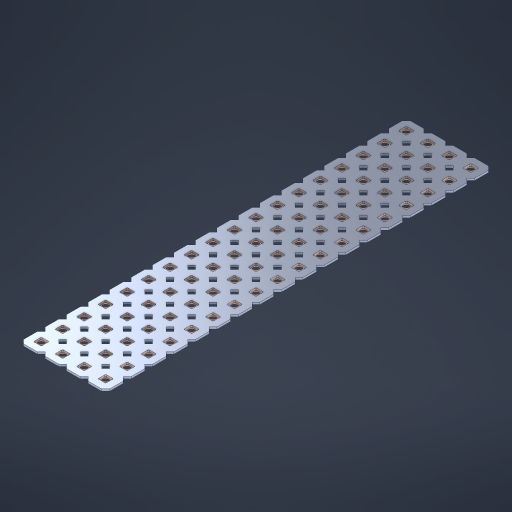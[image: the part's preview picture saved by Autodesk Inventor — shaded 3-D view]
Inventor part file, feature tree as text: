
AUTODESK INVENTOR PART (.ipt)
format: ipt  version: 2023 (Build 270158000, 158)  size: 1,094,144 bytes
history: native  units: in
note: dims shown in document units (in); Inventor stores cm internally (conversion verified against a paired STEP export)
features: other x73, extrude x71, sketch x2, pattern_linear x1
ambient origin geometry x8: Origin, YZ Plane, XZ Plane, XY Plane, X Axis, Y Axis, Z Axis, Center Point
bodies: Solid1 (feature_tree), Body (feature_tree)
feature tree (147):
  pattern_linear  "Rectangular Pattern1"  Spacing1=0.09in  [1 undecoded]
  sketch  "Sketch1"  dims[d1=0.5in]
  sketch  "Sketch2"  dims[d2=0.182in d3=0.09in d4=0.09in d5=0.09in d6=0.09in d7=0.09in d8=0.09in d9=0.09in d10=0.09in d11=0.02in d13=0.0in d14=0.172in d15=0.0625in d16=0.0in d19=0.5in d22=0.5in]
  other  "Srf1"
  other  "Srf126"
  other  "Srf127"
  other  "Srf128"
  other  "Srf129"
  other  "Srf130"
  other  "Srf131"
  other  "Srf250"
  other  "Srf251"
  other  "Srf252"
  other  "Srf253"
  other  "Srf254"
  other  "Srf255"
  other  "Srf256"
  other  "Srf257"
  other  "Srf258"
  other  "Srf259"
  other  "Srf260"
  other  "Srf268"
  other  "Srf269"
  other  "Srf270"
  other  "Srf271"
  other  "Srf272"
  other  "Srf273"
  other  "Srf274"
  other  "Srf275"
  other  "Srf276"
  other  "Srf277"
  other  "Srf278"
  other  "Srf279"
  other  "Srf280"
  other  "Srf281"
  other  "Srf282"
  other  "Srf283"
  other  "Srf284"
  other  "Srf285"
  other  "Srf293"
  other  "Srf294"
  other  "Srf295"
  other  "Srf296"
  other  "Srf297"
  other  "Srf298"
  other  "Srf299"
  other  "Srf300"
  other  "Srf301"
  other  "Srf302"
  other  "Srf303"
  other  "Srf304"
  other  "Srf305"
  other  "Srf306"
  other  "Srf307"
  other  "Srf308"
  other  "Srf309"
  other  "Srf310"
  other  "Srf318"
  other  "Srf319"
  other  "Srf320"
  other  "Srf321"
  other  "Srf322"
  other  "Srf323"
  other  "Srf324"
  other  "Srf325"
  other  "Srf326"
  other  "Srf327"
  other  "Srf328"
  other  "Srf329"
  other  "Srf330"
  other  "Srf331"
  other  "Srf332"
  other  "Srf333"
  other  "Srf334"
  other  "Srf335"
  other  "Circle"
  extrude  "ExtrusionSrf126"  Depth=0.09in
  extrude  "ExtrusionSrf127"  Depth=0.09in
  extrude  "ExtrusionSrf128"  Depth=0.09in
  extrude  "ExtrusionSrf129"  Depth=0.09in
  extrude  "ExtrusionSrf130"  Depth=0.09in
  extrude  "ExtrusionSrf131"  Depth=0.09in
  extrude  "ExtrusionSrf250"  Depth=0.09in
  extrude  "ExtrusionSrf251"  Depth=0.02in
  extrude  "ExtrusionSrf252"  TaperAngle=0.0deg  [1 undecoded]
  extrude  "ExtrusionSrf253"  Depth=0.5in
  extrude  "ExtrusionSrf254"  Depth=0.5in TaperAngle=0.0deg
  extrude  "ExtrusionSrf255"  Depth=0.5in
  extrude  "ExtrusionSrf256"  Depth=0.5in
  extrude  "ExtrusionSrf257"  [1 undecoded]
  extrude  "ExtrusionSrf258"  [1 undecoded]
  extrude  "ExtrusionSrf259"  [1 undecoded]
  extrude  "ExtrusionSrf260"  [1 undecoded]
  extrude  "ExtrusionSrf268"  [1 undecoded]
  extrude  "ExtrusionSrf269"  [1 undecoded]
  extrude  "ExtrusionSrf270"  [1 undecoded]
  extrude  "ExtrusionSrf271"  [1 undecoded]
  extrude  "ExtrusionSrf272"  [1 undecoded]
  extrude  "ExtrusionSrf273"  [1 undecoded]
  extrude  "ExtrusionSrf274"  [1 undecoded]
  extrude  "ExtrusionSrf275"  [1 undecoded]
  extrude  "ExtrusionSrf276"  [1 undecoded]
  extrude  "ExtrusionSrf277"  [1 undecoded]
  extrude  "ExtrusionSrf278"  [1 undecoded]
  extrude  "ExtrusionSrf279"  [1 undecoded]
  extrude  "ExtrusionSrf280"  [1 undecoded]
  extrude  "ExtrusionSrf281"  [1 undecoded]
  extrude  "ExtrusionSrf282"  [1 undecoded]
  extrude  "ExtrusionSrf283"  [1 undecoded]
  extrude  "ExtrusionSrf284"  [1 undecoded]
  extrude  "ExtrusionSrf285"  [1 undecoded]
  extrude  "ExtrusionSrf293"  [1 undecoded]
  extrude  "ExtrusionSrf294"  [1 undecoded]
  extrude  "ExtrusionSrf295"  [1 undecoded]
  extrude  "ExtrusionSrf296"  [1 undecoded]
  extrude  "ExtrusionSrf297"  [1 undecoded]
  extrude  "ExtrusionSrf298"  [1 undecoded]
  extrude  "ExtrusionSrf299"  [1 undecoded]
  extrude  "ExtrusionSrf300"  [1 undecoded]
  extrude  "ExtrusionSrf301"  [1 undecoded]
  extrude  "ExtrusionSrf302"  [1 undecoded]
  extrude  "ExtrusionSrf303"  [1 undecoded]
  extrude  "ExtrusionSrf304"  [1 undecoded]
  extrude  "ExtrusionSrf305"  [1 undecoded]
  extrude  "ExtrusionSrf306"  [1 undecoded]
  extrude  "ExtrusionSrf307"  [1 undecoded]
  extrude  "ExtrusionSrf308"  [1 undecoded]
  extrude  "ExtrusionSrf309"  [1 undecoded]
  extrude  "ExtrusionSrf310"  [1 undecoded]
  extrude  "ExtrusionSrf318"  [1 undecoded]
  extrude  "ExtrusionSrf319"  [1 undecoded]
  extrude  "ExtrusionSrf320"  [1 undecoded]
  extrude  "ExtrusionSrf321"  [1 undecoded]
  extrude  "ExtrusionSrf322"  [1 undecoded]
  extrude  "ExtrusionSrf323"  [1 undecoded]
  extrude  "ExtrusionSrf324"  [1 undecoded]
  extrude  "ExtrusionSrf325"  [1 undecoded]
  extrude  "ExtrusionSrf326"  [1 undecoded]
  extrude  "ExtrusionSrf327"  [1 undecoded]
  extrude  "ExtrusionSrf328"  [1 undecoded]
  extrude  "ExtrusionSrf329"  [1 undecoded]
  extrude  "ExtrusionSrf330"  [1 undecoded]
  extrude  "ExtrusionSrf331"  [1 undecoded]
  extrude  "ExtrusionSrf332"  [1 undecoded]
  extrude  "ExtrusionSrf333"  [1 undecoded]
  extrude  "ExtrusionSrf334"  [1 undecoded]
  extrude  "ExtrusionSrf335"  [1 undecoded]
note: 60 required parameter values undecoded (feature->parameter linkage not recoverable at this tier; creation-order binding heuristic only, values carry confidence <= 0.55)
